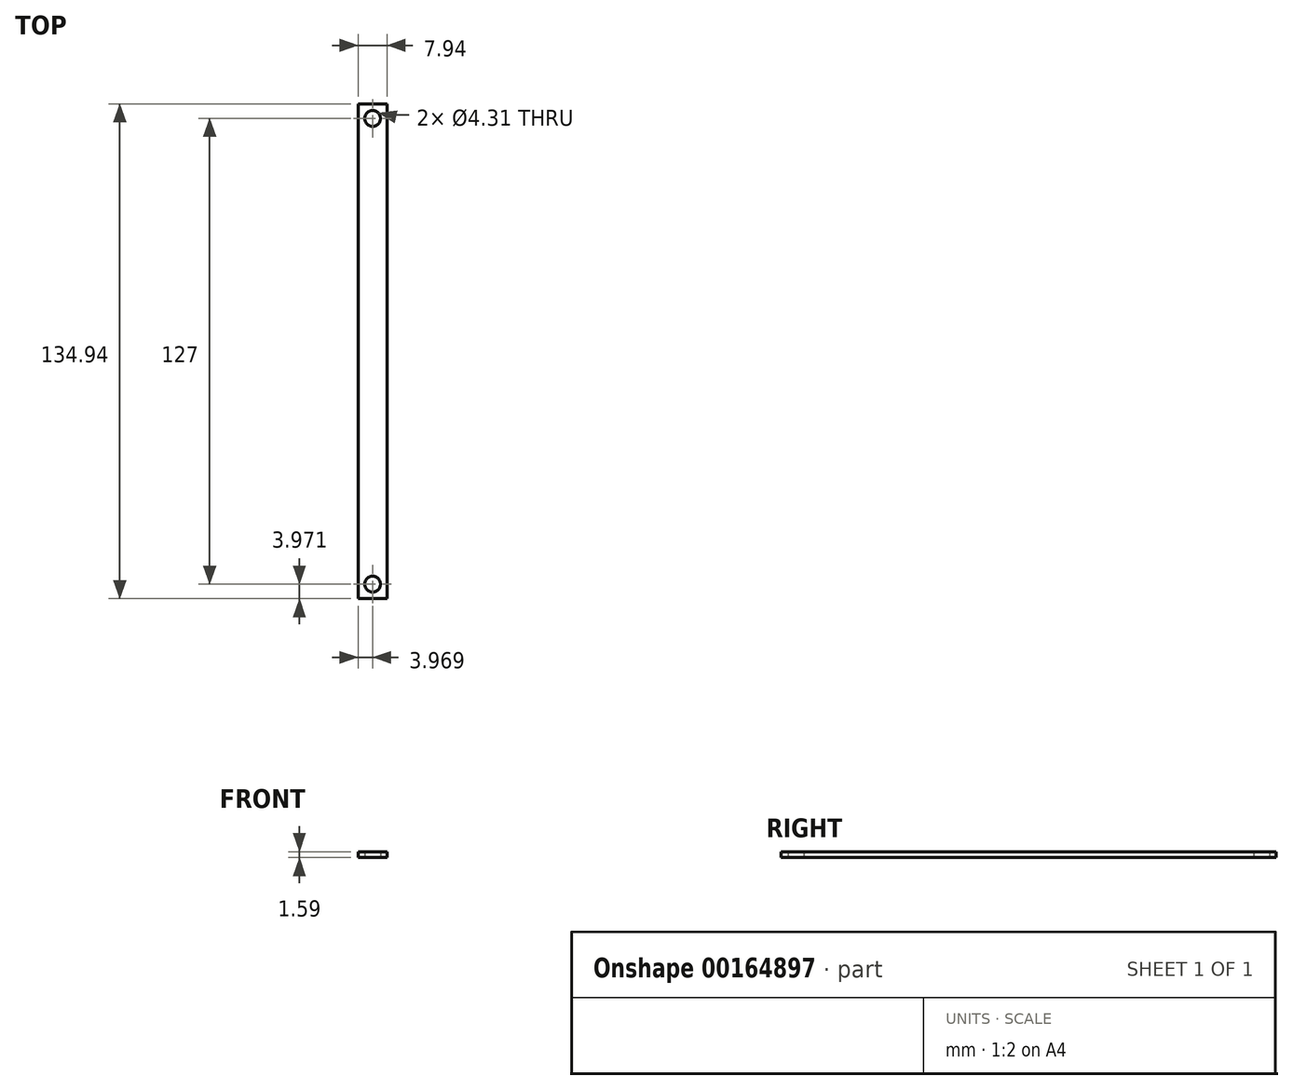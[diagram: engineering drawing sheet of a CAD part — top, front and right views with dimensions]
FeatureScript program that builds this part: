
annotation { "Feature Type Name" : "Feature", "Feature Type Description" : "" }
export const myFeature = defineFeature(function(context is Context, id is Id, definition is map)
    precondition{}
    {
        {
            var Q0;
            Q0=qCreatedBy(makeId("Top.planeOp"),FACE);
            var sketch = newSketch(context, id + "F0", { "sketchPlane" : qUnion([Q0])});
            skLineSegment(sketch, "E0.bottom", {"start": v(0, 0) * mm, "end": v(7.94, 0) * mm});
            skLineSegment(sketch, "E0.top", {"start": v(0, -134.94) * mm, "end": v(7.94, -134.94) * mm});
            skLineSegment(sketch, "E0.left", {"start": v(0, 0) * mm, "end": v(0, -134.94) * mm});
            skLineSegment(sketch, "E0.right", {"start": v(7.94, 0) * mm, "end": v(7.94, -134.94) * mm});
            skLineSegment(sketch, "E1", {"start": v(3.97, 0) * mm, "end": v(3.97, -3.97) * mm, "construction": true});
            skLineSegment(sketch, "E2", {"start": v(3.97, -3.97) * mm, "end": v(7.94, -3.97) * mm, "construction": true});
            skLineSegment(sketch, "E3", {"start": v(3.97, -134.94) * mm, "end": v(3.97, -130.97) * mm, "construction": true});
            skCircle(sketch, "E4", {"center": v(3.97, -3.97) * mm, "radius": 2.15 * mm});
            skCircle(sketch, "E5", {"center": v(3.97, -130.97) * mm, "radius": 2.15 * mm});
            skSolve(sketch);
        }
        {
            var Q0;
            Q0 = qSketchRegion(id + "F0", true);
            extrude(context, id + "F1", {"entities" : qUnion([Q0]), "depth" : 1.59 * mm});
        }
    });
